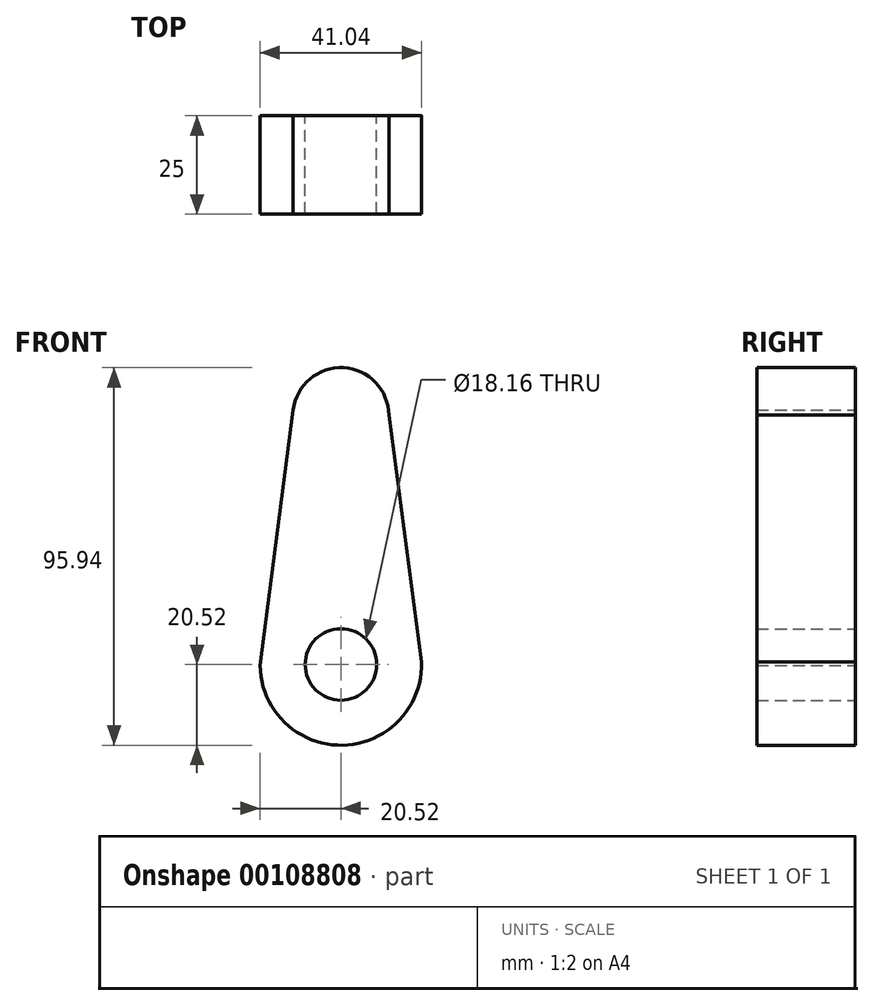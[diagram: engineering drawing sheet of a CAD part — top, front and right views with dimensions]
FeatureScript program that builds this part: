
annotation { "Feature Type Name" : "Feature", "Feature Type Description" : "" }
export const myFeature = defineFeature(function(context is Context, id is Id, definition is map)
    precondition{}
    {
        {
            var Q0;
            Q0=qCreatedBy(makeId("Front.planeOp"),FACE);
            var sketch = newSketch(context, id + "F0", { "sketchPlane" : qUnion([Q0])});
            skCircle(sketch, "E0", {"center": v(0, 0) * mm, "radius": 20.52 * mm});
            skCircle(sketch, "E1", {"center": v(0, 63.24) * mm, "radius": 12.18 * mm});
            skLineSegment(sketch, "E2", {"start": v(-12.1, 64.67) * mm, "end": v(-20.52, -0.3) * mm});
            skLineSegment(sketch, "E3", {"start": v(12.18, 63.32) * mm, "end": v(20.51, 0.58) * mm});
            skSolve(sketch);
        }
        {
            var Q0;
            {var subQ0=sQuery(id+"F0.wireOp",EDGE,"E3");var subQ1=sQuery(id+"F0.wireOp",EDGE,"E0");var subQ2=makeQuery(id+"F0.imprint","INTERSECT",VERTEX,{"disambiguationData":[OD(1.0)],"derivedFrom":[subQ1,subQ0]});Q0=makeQuery(id+"F0.imprint","IMPRINT",FACE,{"disambiguationData":[TD([[makeQuery(id+"F0.imprint","IMPRINT",EDGE,{"disambiguationData":[TD([[subQ2,-1.0]])],"derivedFrom":subQ1}),-1.0]])]});}
            var Q1;
            {var subQ0=sQuery(id+"F0.wireOp",EDGE,"E3");var subQ1=sQuery(id+"F0.wireOp",EDGE,"E0");var subQ2=makeQuery(id+"F0.imprint","INTERSECT",VERTEX,{"disambiguationData":[OD(1.0)],"derivedFrom":[subQ1,subQ0]});Q1=makeQuery(id+"F0.imprint","IMPRINT",FACE,{"disambiguationData":[TD([[makeQuery(id+"F0.imprint","IMPRINT",EDGE,{"disambiguationData":[TD([[subQ2,-1.0]])],"derivedFrom":subQ1}),1.0]])]});}
            var Q2;
            {var subQ0=sQuery(id+"F0.wireOp",EDGE,"E1");var subQ1=makeQuery(id+"F0.imprint","INTERSECT",VERTEX,{"derivedFrom":[subQ0,sQuery(id+"F0.wireOp",EDGE,"E2")]});Q2=makeQuery(id+"F0.imprint","IMPRINT",FACE,{"disambiguationData":[TD([[makeQuery(id+"F0.imprint","IMPRINT",EDGE,{"disambiguationData":[TD([[subQ1,1.0]])],"derivedFrom":subQ0}),1.0]])]});}
            extrude(context, id + "F3", {"entities" : qUnion([Q0, Q1, Q2]), "depth" : 25 * mm});
        }
        {
            var Q0;
            Q0=qCreatedBy(makeId("Front.planeOp"),FACE);
            var sketch = newSketch(context, id + "F4", { "sketchPlane" : qUnion([Q0])});
            skCircle(sketch, "E4", {"center": v(0, 0) * mm, "radius": 9.08 * mm});
            skSolve(sketch);
        }
        {
            var Q0;
            Q0 = qSketchRegion(id + "F4", true);
            extrude(context, id + "F1", {"entities" : qUnion([Q0]), "operationType" : NewBodyOperationType.REMOVE, "endBound" : BoundingType.THROUGH_ALL, "depth" : 25 * mm});
        }
    });
